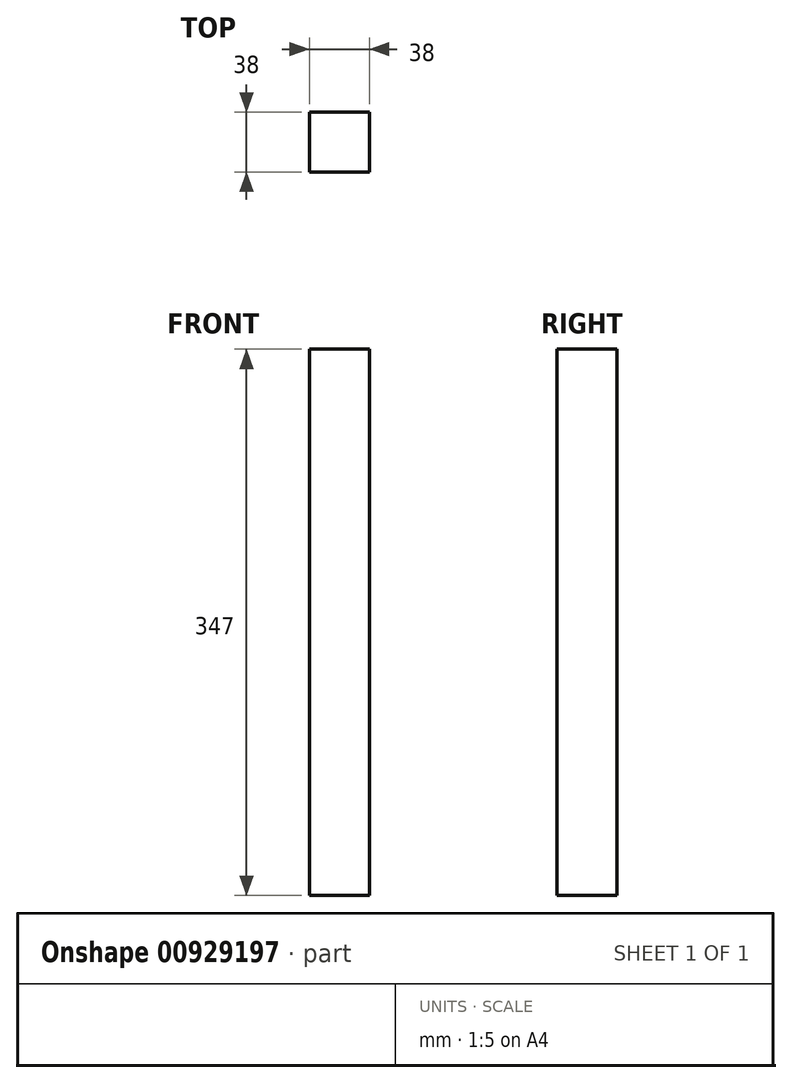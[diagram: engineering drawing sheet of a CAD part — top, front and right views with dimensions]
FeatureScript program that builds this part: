
annotation { "Feature Type Name" : "Feature", "Feature Type Description" : "" }
export const myFeature = defineFeature(function(context is Context, id is Id, definition is map)
    precondition{}
    {
        {
            var Q0;
            Q0=qCreatedBy(makeId("Front.planeOp"),FACE);
            var sketch = newSketch(context, id + "F0", { "sketchPlane" : qUnion([Q0])});
            skLineSegment(sketch, "E0.bottom", {"start": v(-24.87, 284.07) * mm, "end": v(13.13, 284.07) * mm});
            skLineSegment(sketch, "E0.top", {"start": v(-24.87, -62.93) * mm, "end": v(13.13, -62.93) * mm});
            skLineSegment(sketch, "E0.left", {"start": v(-24.87, 284.07) * mm, "end": v(-24.87, -62.93) * mm});
            skLineSegment(sketch, "E0.right", {"start": v(13.13, 284.07) * mm, "end": v(13.13, -62.93) * mm});
            skSolve(sketch);
        }
        {
            var Q0;
            Q0=qSketchRegion(id+"F0",true);
            extrude(context, id + "F1", {"entities" : qUnion([Q0]), "depth" : 38 * mm, "offsetDistance" : 25 * mm});
        }
    });
